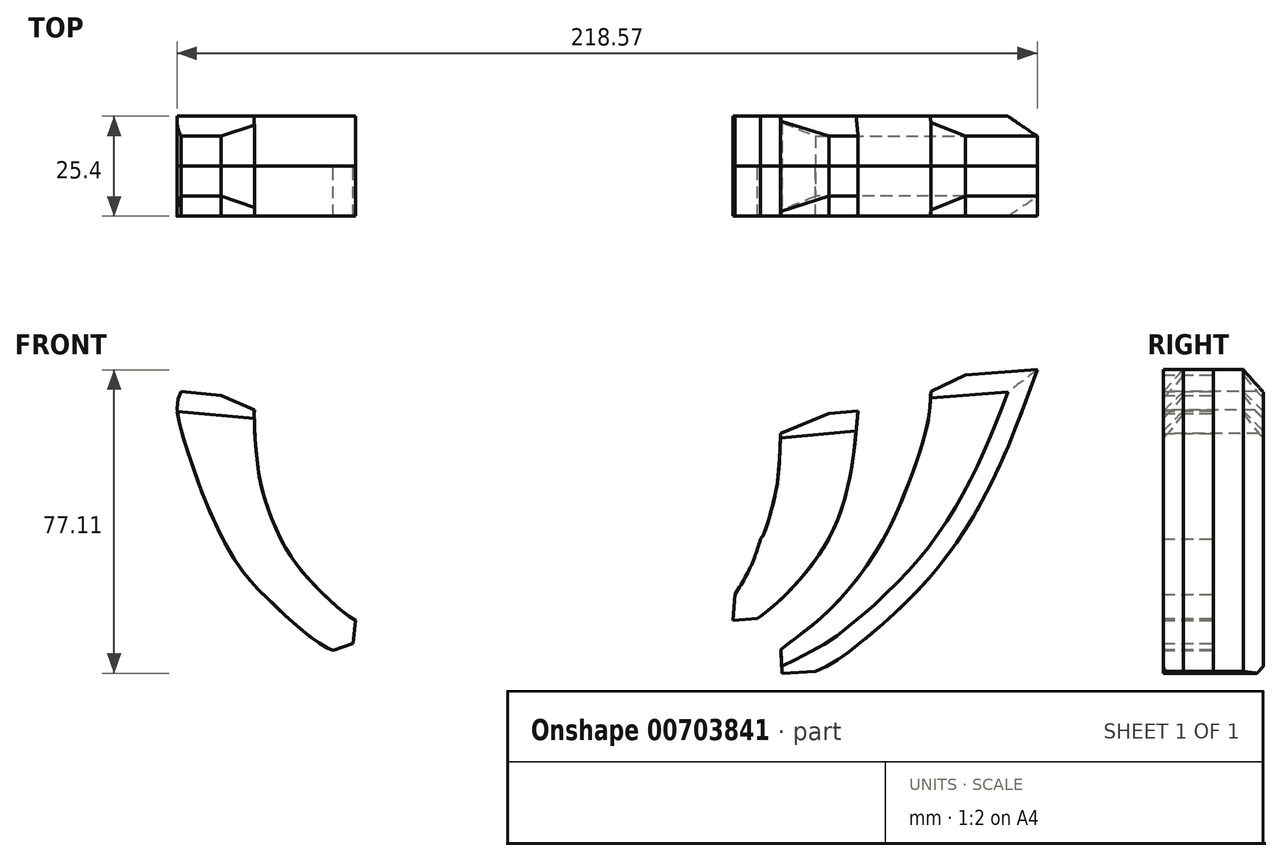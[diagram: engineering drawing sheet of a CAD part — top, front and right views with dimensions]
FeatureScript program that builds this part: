
annotation { "Feature Type Name" : "Feature", "Feature Type Description" : "" }
export const myFeature = defineFeature(function(context is Context, id is Id, definition is map)
    precondition{}
    {
        {
            var Q0;
            Q0=qCreatedBy(makeId("Front.planeOp"),FACE);
            var sketch = newSketch(context, id + "F0", { "sketchPlane" : qUnion([Q0])});
            skLineSegment(sketch, "E0", {"start": v(-122.31, 49.69) * mm, "end": v(-103.8, 48.16) * mm});
            skLineSegment(sketch, "E1", {"start": v(-103.8, 48.16) * mm, "end": v(-95.32, 44.06) * mm});
            skLineSegment(sketch, "E2", {"start": v(-95.32, 44.06) * mm, "end": v(-85.2, 43.1) * mm});
            skLineSegment(sketch, "E3", {"start": v(-85.2, 43.1) * mm, "end": v(-76.71, 39.38) * mm});
            skLineSegment(sketch, "E4", {"start": v(-76.71, 39.38) * mm, "end": v(-68.96, 38.36) * mm});
            skLineSegment(sketch, "E5", {"start": v(-68.96, 38.36) * mm, "end": v(-57.43, 33.63) * mm});
            skFitSpline(sketch, "E6", {"points": [v(-57.43, 33.63) * mm, v(-56.85, 26.65) * mm, v(-56.16, 19.73) * mm, v(-55.33, 15.7) * mm, v(-54.2, 11.73) * mm, v(-52.95, 8.15) * mm, v(-51.8, 6.64) * mm], "startDerivative": vector(2.75, -32.82) * mm, "endDerivative": vector(10.96, -11.97) * mm});
            skFitSpline(sketch, "E7", {"points": [v(-122.31, 49.69) * mm, v(-114.04, 28.95) * mm, v(-106.9, 14.55) * mm, v(-96.83, 0) * mm, v(-86.28, -11.6) * mm, v(-75.84, -20.58) * mm, v(-65.88, -27.11) * mm], "startDerivative": vector(42.95, -111.11) * mm, "endDerivative": vector(69.64, -42.92) * mm});
            skLineSegment(sketch, "E8", {"start": v(-65.88, -27.11) * mm, "end": v(-57.47, -27.11) * mm});
            skLineSegment(sketch, "E9", {"start": v(-57.47, -27.11) * mm, "end": v(-56.75, -21.74) * mm});
            skLineSegment(sketch, "E10", {"start": v(-56.75, -21.74) * mm, "end": v(-51.68, -19.86) * mm});
            skLineSegment(sketch, "E11", {"start": v(-51.68, -19.86) * mm, "end": v(-51.05, -14.03) * mm});
            skLineSegment(sketch, "E12", {"start": v(-51.05, -14.03) * mm, "end": v(-45.06, -14.03) * mm});
            skLineSegment(sketch, "E13", {"start": v(-45.06, -14.03) * mm, "end": v(-45.06, -8.46) * mm});
            skLineSegment(sketch, "E14", {"start": v(122.2, 49.63) * mm, "end": v(104, 48.25) * mm});
            skLineSegment(sketch, "E15", {"start": v(104, 48.25) * mm, "end": v(95.13, 44.09) * mm});
            skLineSegment(sketch, "E16", {"start": v(95.13, 44.09) * mm, "end": v(84.88, 43.17) * mm});
            skLineSegment(sketch, "E17", {"start": v(84.88, 43.17) * mm, "end": v(76.66, 39.2) * mm});
            skLineSegment(sketch, "E18", {"start": v(76.66, 39.2) * mm, "end": v(69.2, 38.51) * mm});
            skLineSegment(sketch, "E19", {"start": v(69.2, 38.51) * mm, "end": v(56.96, 33.46) * mm});
            skFitSpline(sketch, "E20", {"points": [v(56.96, 33.46) * mm, v(56.22, 21.38) * mm, v(54.75, 14.45) * mm, v(52.8, 8.08) * mm, v(51.9, 6.62) * mm], "startDerivative": vector(-1.32, -37.72) * mm, "endDerivative": vector(-6.66, -8.71) * mm});
            skFitSpline(sketch, "E21", {"points": [v(122.2, 49.63) * mm, v(115.67, 32.4) * mm, v(107.79, 15.56) * mm, v(101.55, 5.56) * mm, v(95.31, -2.56) * mm, v(87.2, -11.03) * mm, v(79.66, -17.74) * mm, v(71.9, -23.74) * mm, v(65.9, -27.08) * mm], "startDerivative": vector(-39.57, -109.68) * mm, "endDerivative": vector(-61.7, -30.96) * mm});
            skLineSegment(sketch, "E22", {"start": v(65.9, -27.08) * mm, "end": v(57.32, -27.48) * mm});
            skLineSegment(sketch, "E23", {"start": v(57.32, -27.48) * mm, "end": v(57.03, -21.4) * mm});
            skLineSegment(sketch, "E24", {"start": v(57.03, -21.4) * mm, "end": v(51.88, -20.45) * mm});
            skLineSegment(sketch, "E25", {"start": v(51.88, -20.45) * mm, "end": v(51.12, -13.55) * mm});
            skLineSegment(sketch, "E26", {"start": v(51.12, -13.55) * mm, "end": v(44.82, -14.1) * mm});
            skLineSegment(sketch, "E27", {"start": v(44.82, -14.1) * mm, "end": v(45.4, -7.48) * mm});
            skFitSpline(sketch, "E28", {"points": [v(-51.8, 6.64) * mm, v(-48.35, -1.52) * mm, v(-45.06, -8.46) * mm], "startDerivative": vector(6.64, -16.1) * mm, "endDerivative": vector(6.86, -14.06) * mm});
            skFitSpline(sketch, "E29", {"points": [v(51.9, 6.62) * mm, v(49.56, 0) * mm, v(45.4, -7.48) * mm], "startDerivative": vector(-4.2, -13.85) * mm, "endDerivative": vector(-8.72, -14.35) * mm});
            skSolve(sketch);
        }
        {
            var Q0;
            Q0=makeQuery(id+"F0.imprint","IMPRINT",FACE,{"disambiguationData":[TD([[makeQuery(id+"F0.imprint","IMPRINT",EDGE,{"derivedFrom":sQuery(id+"F0.wireOp",EDGE,"E0")}),-1.0]])]});
            var Q1;
            Q1=makeQuery(id+"F0.imprint","IMPRINT",FACE,{"disambiguationData":[TD([[makeQuery(id+"F0.imprint","IMPRINT",EDGE,{"derivedFrom":sQuery(id+"F0.wireOp",EDGE,"E14")}),1.0]])]});
            extrude(context, id + "F1", {"entities" : qUnion([Q0, Q1]), "depth" : 12.7 * mm, "offsetDistance" : 25.4 * mm});
        }
        {
            var Q0;
            Q0=makeQuery(id+"F1.opExtrude","CAP_FACE",FACE,{"disambiguationData":[OSD([sQuery(id+"F0.wireOp",EDGE,"E0"),sQuery(id+"F0.wireOp",EDGE,"E1"),sQuery(id+"F0.wireOp",EDGE,"E2"),sQuery(id+"F0.wireOp",EDGE,"E3"),sQuery(id+"F0.wireOp",EDGE,"E4"),sQuery(id+"F0.wireOp",EDGE,"E5"),sQuery(id+"F0.wireOp",EDGE,"E6"),sQuery(id+"F0.wireOp",EDGE,"E7"),sQuery(id+"F0.wireOp",EDGE,"E8"),sQuery(id+"F0.wireOp",EDGE,"E9"),sQuery(id+"F0.wireOp",EDGE,"E10"),sQuery(id+"F0.wireOp",EDGE,"E11"),sQuery(id+"F0.wireOp",EDGE,"E12"),sQuery(id+"F0.wireOp",EDGE,"E13"),sQuery(id+"F0.wireOp",EDGE,"E28")])],"isStart":false});
            var Q1;
            Q1=makeQuery(id+"F1.opExtrude","CAP_FACE",FACE,{"disambiguationData":[OSD([sQuery(id+"F0.wireOp",EDGE,"E14"),sQuery(id+"F0.wireOp",EDGE,"E15"),sQuery(id+"F0.wireOp",EDGE,"E16"),sQuery(id+"F0.wireOp",EDGE,"E17"),sQuery(id+"F0.wireOp",EDGE,"E18"),sQuery(id+"F0.wireOp",EDGE,"E19"),sQuery(id+"F0.wireOp",EDGE,"E20"),sQuery(id+"F0.wireOp",EDGE,"E21"),sQuery(id+"F0.wireOp",EDGE,"E22"),sQuery(id+"F0.wireOp",EDGE,"E23"),sQuery(id+"F0.wireOp",EDGE,"E24"),sQuery(id+"F0.wireOp",EDGE,"E25"),sQuery(id+"F0.wireOp",EDGE,"E26"),sQuery(id+"F0.wireOp",EDGE,"E27"),sQuery(id+"F0.wireOp",EDGE,"E29")])],"isStart":false});
            extrude(context, id + "F2", {"entities" : qUnion([Q0, Q1]), "oppositeDirection" : true, "depth" : 25.4 * mm, "offsetDistance" : 25.4 * mm});
        }
        {
            var Q0;
            Q0=makeQuery(id+"F2.opExtrude","CAP_FACE",FACE,{"disambiguationData":[OSD([sQuery(id+"F0.wireOp",EDGE,"E14"),sQuery(id+"F0.wireOp",EDGE,"E15"),sQuery(id+"F0.wireOp",EDGE,"E16"),sQuery(id+"F0.wireOp",EDGE,"E17"),sQuery(id+"F0.wireOp",EDGE,"E18"),sQuery(id+"F0.wireOp",EDGE,"E19"),sQuery(id+"F0.wireOp",EDGE,"E20"),sQuery(id+"F0.wireOp",EDGE,"E21"),sQuery(id+"F0.wireOp",EDGE,"E22"),sQuery(id+"F0.wireOp",EDGE,"E23"),sQuery(id+"F0.wireOp",EDGE,"E24"),sQuery(id+"F0.wireOp",EDGE,"E25"),sQuery(id+"F0.wireOp",EDGE,"E26"),sQuery(id+"F0.wireOp",EDGE,"E27"),sQuery(id+"F0.wireOp",EDGE,"E29")])],"isStart":false});
            var sketch = newSketch(context, id + "F3", { "sketchPlane" : qUnion([Q0])});
            skFitSpline(sketch, "E30", {"points": [v(-76.66, 39.2) * mm, v(-75.08, 25.26) * mm, v(-71.57, 11.76) * mm, v(-64.87, 0) * mm, v(-55.73, -9.93) * mm, v(-51.12, -13.55) * mm], "startDerivative": vector(5.7, -64.2) * mm, "endDerivative": vector(30.19, -21.67) * mm});
            skFitSpline(sketch, "E31", {"points": [v(-95.13, 44.09) * mm, v(-94.28, 35.68) * mm, v(-89, 19.48) * mm, v(-81.68, 4.14) * mm, v(-70.92, -9.87) * mm, v(-62.77, -17.08) * mm, v(-57.03, -21.4) * mm], "startDerivative": vector(1.9, -56.55) * mm, "endDerivative": vector(44.32, -32.83) * mm});
            skSolve(sketch);
        }
        {
            var Q0;
            Q0=makeQuery(id+"F2.opExtrude","CAP_FACE",FACE,{"disambiguationData":[OSD([sQuery(id+"F0.wireOp",EDGE,"E0"),sQuery(id+"F0.wireOp",EDGE,"E1"),sQuery(id+"F0.wireOp",EDGE,"E2"),sQuery(id+"F0.wireOp",EDGE,"E3"),sQuery(id+"F0.wireOp",EDGE,"E4"),sQuery(id+"F0.wireOp",EDGE,"E5"),sQuery(id+"F0.wireOp",EDGE,"E6"),sQuery(id+"F0.wireOp",EDGE,"E7"),sQuery(id+"F0.wireOp",EDGE,"E8"),sQuery(id+"F0.wireOp",EDGE,"E9"),sQuery(id+"F0.wireOp",EDGE,"E10"),sQuery(id+"F0.wireOp",EDGE,"E11"),sQuery(id+"F0.wireOp",EDGE,"E12"),sQuery(id+"F0.wireOp",EDGE,"E13"),sQuery(id+"F0.wireOp",EDGE,"E28")])],"isStart":false});
            var sketch = newSketch(context, id + "F4", { "sketchPlane" : qUnion([Q0])});
            skFitSpline(sketch, "E32", {"points": [v(95.32, 44.06) * mm, v(96.37, 40.15) * mm, v(93, 26.9) * mm, v(88.3, 14.26) * mm, v(80.83, 0) * mm, v(74.33, -7.54) * mm, v(66.38, -15) * mm, v(59.64, -20.18) * mm, v(56.75, -21.74) * mm], "startDerivative": vector(19.35, -39.65) * mm, "endDerivative": vector(-35.72, -17.16) * mm});
            skFitSpline(sketch, "E33", {"points": [v(76.71, 39.38) * mm, v(76.71, 37.02) * mm, v(75.69, 24.01) * mm, v(72.57, 12.56) * mm, v(67.74, 2.63) * mm, v(61.87, -4.66) * mm, v(55.16, -11.1) * mm, v(51.05, -14.03) * mm], "startDerivative": vector(0.5, -24.06) * mm, "endDerivative": vector(-35.03, -22.95) * mm});
            skSolve(sketch);
        }
        {
            var Q0;
            Q0=makeQuery(id+"F3.imprint","IMPRINT",FACE,{"disambiguationData":[TD([[makeQuery(id+"F3.imprint","IMPRINT",EDGE,{"derivedFrom":sQuery(id+"F3.wireOp",EDGE,"E30")}),-1.0]])]});
            extrude(context, id + "F5", {"entities" : qUnion([Q0]), "operationType" : NewBodyOperationType.REMOVE, "oppositeDirection" : true, "depth" : 25.4 * mm, "offsetDistance" : 25.4 * mm});
        }
        {
            var Q0;
            Q0=makeQuery(id+"F4.imprint","IMPRINT",FACE,{"disambiguationData":[TD([[makeQuery(id+"F4.imprint","IMPRINT",EDGE,{"derivedFrom":sQuery(id+"F4.wireOp",EDGE,"E33")}),-1.0]])]});
            var Q1;
            Q1=makeQuery(id+"F4.imprint","IMPRINT",FACE,{"disambiguationData":[TD([[makeQuery(id+"F4.imprint","IMPRINT",EDGE,{"derivedFrom":sQuery(id+"F4.wireOp",EDGE,"E32")}),1.0]])]});
            extrude(context, id + "F6", {"entities" : qUnion([Q0, Q1]), "operationType" : NewBodyOperationType.REMOVE, "oppositeDirection" : true, "depth" : 25.4 * mm, "offsetDistance" : 25.4 * mm});
        }
        {
            var Q0;
            Q0=makeQuery(id+"F5.boolean.opBoolean","COPY",EDGE,{"derivedFrom":makeQuery(id+"F5.opExtrude","CAP_EDGE",EDGE,{"disambiguationData":[OSD([sQuery(id+"F3.wireOp",EDGE,"E30")])],"isStart":true})});
            var Q1;
            Q1=makeQuery(id+"F2.opExtrude","CAP_EDGE",EDGE,{"disambiguationData":[OSD([sQuery(id+"F0.wireOp",EDGE,"E18")])],"isStart":false});
            chamfer(context, id + "F7", {"entities" : qUnion([Q0, Q1]), "width" : 5.08 * mm, "tangentPropagation" : true});
        }
        {
            var Q0;
            Q0=makeQuery(id+"F2.opExtrude","CAP_EDGE",EDGE,{"disambiguationData":[OSD([sQuery(id+"F0.wireOp",EDGE,"E21")])],"isStart":false});
            var Q1;
            Q1=makeQuery(id+"F2.opExtrude","CAP_EDGE",EDGE,{"disambiguationData":[OSD([sQuery(id+"F0.wireOp",EDGE,"E14")])],"isStart":false});
            chamfer(context, id + "F8", {"entities" : qUnion([Q0, Q1]), "width" : 5.08 * mm, "tangentPropagation" : true});
        }
        {
            var Q0;
            Q0=makeQuery(id+"F6.boolean.opBoolean","COPY",EDGE,{"derivedFrom":makeQuery(id+"F6.opExtrude","CAP_EDGE",EDGE,{"disambiguationData":[OSD([sQuery(id+"F4.wireOp",EDGE,"E32")])],"isStart":true})});
            var Q1;
            Q1=makeQuery(id+"F2.opExtrude","CAP_EDGE",EDGE,{"disambiguationData":[OSD([sQuery(id+"F0.wireOp",EDGE,"E2")])],"isStart":false});
            chamfer(context, id + "F9", {"entities" : qUnion([Q0, Q1]), "width" : 5.08 * mm, "tangentPropagation" : true});
        }
        {
            var Q0;
            Q0=makeQuery(id+"F2.opExtrude","CAP_EDGE",EDGE,{"disambiguationData":[OSD([sQuery(id+"F0.wireOp",EDGE,"E21")])],"isStart":true});
            var Q1;
            Q1=makeQuery(id+"F2.opExtrude","CAP_EDGE",EDGE,{"disambiguationData":[OSD([sQuery(id+"F0.wireOp",EDGE,"E14")])],"isStart":true});
            var Q2;
            Q2=makeQuery(id+"F2.opExtrude","CAP_EDGE",EDGE,{"disambiguationData":[OSD([sQuery(id+"F0.wireOp",EDGE,"E18")])],"isStart":true});
            var Q3;
            Q3=makeQuery(id+"F5.boolean.opBoolean","COPY",EDGE,{"derivedFrom":makeQuery(id+"F5.opExtrude","CAP_EDGE",EDGE,{"disambiguationData":[OSD([sQuery(id+"F3.wireOp",EDGE,"E30")])],"isStart":false})});
            var Q4;
            Q4=makeQuery(id+"F2.opExtrude","CAP_EDGE",EDGE,{"disambiguationData":[OSD([sQuery(id+"F0.wireOp",EDGE,"E2")])],"isStart":true});
            var Q5;
            Q5=makeQuery(id+"F6.boolean.opBoolean","COPY",EDGE,{"derivedFrom":makeQuery(id+"F6.opExtrude","CAP_EDGE",EDGE,{"disambiguationData":[OSD([sQuery(id+"F4.wireOp",EDGE,"E32")])],"isStart":false})});
            chamfer(context, id + "F10", {"entities" : qUnion([Q0, Q1, Q2, Q3, Q4, Q5]), "width" : 5.08 * mm, "tangentPropagation" : true});
        }
    });
